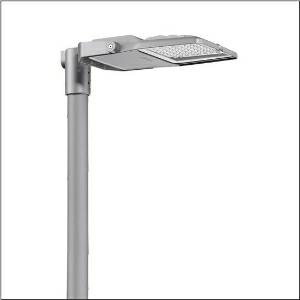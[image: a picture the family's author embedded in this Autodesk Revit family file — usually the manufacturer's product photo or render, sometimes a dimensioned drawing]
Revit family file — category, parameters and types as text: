
# Revit family: floodlight_fl_21_mini___pl52_5xa7776c2d3a_1d2c
name_source: partatom
category: Lighting Fixtures
units: mm (PartAtom-declared; Revit-internal decimal feet)

## family parameters
Cut with Voids When Loaded = No
Host = Face
Light Source = No
Part Type = Normal
Room Calculation Point = No
Round Connector Dimension = Use Diameter
Shared = No

## types (1)
- --- (1 x LED, 12190 lm, 89 W, 3000K)
    Apparent Load = 89 VA
    CIE Flux Codes = 26 60 98 100 100
    Color Rendering = 70
    Color Temperature = 3000K
    Default Elevation = 1800 mm
    Description = Floodlight FL 21 mini, floodlight, primary light control with lens, of PMMA, primary optical cover: protective disc, of toughened safety glass, transparent, light distribution: PL52, light emission: direct distribution, installation type: surface-mounted, LED, High Power LED, rated luminous flux: 12.190lm, luminous efficacy: 137lm/W, light colour: 730, colour temperature: 3000K, control gear: Smart Interface (Zhaga), control: flexible luminous flux parameterisation, time-dependent luminous flux control, constant luminous flux control, overheat protection, pre-setting: logarithmic dimming characteristic, with terminal, 6-pole, mains connection: 220..240V, AC, 50/60Hz, start of lifetime: 89W, end of service life: 94W, reduction: 43W, luminaire housing, of diecast aluminium, powder-coated, SITECO metallic grey (DB 702S), corrosivity category C5 mid according to DIN EN ISO 12944, suitable for swimming pools, chlorine-resistant, sealing non-destructively replaceable, please order mast flange separately, mast bracket, of steel, galvanised, powder-coated, SITECO metallic grey (DB 702S), Smart Interface below and above, protection rating (complete): IP66, insulation class (complete): insulation class II (safety insulation), certification: CE, ENEC, VDE, protection symbol: D, impact resistance: IK08, permissible operating ambient temperature: -40..+40°C, permissible operating ambient temperature for outdoor applications: -40..+50°C, standard: DIN EN 12944, LABS conformity tested according to VDMA 24364:2018-05, packaging unit: 1 piece

Light Distribution: PL52
    Height = 70 mm
    Lamp = 1 x LED
    Lamp Light Flux = 12190 lm
    Lamp Power = 89 W
    Lamp count = 1
    Length = 485 mm
    Luminous efficacy = 137 lm/W
    Manufacturer = Siteco
    ModVariant = No
    Model = 5XA7776C2D3A
    Number of Poles = 1
    OnlyDefault = Yes
    Power Factor = 1
    Product Name = Floodlight FL 21 mini | PL52
    Product group = floodlight | pylon annexe
    ProductGroupID = 6201
    Protection Class = Protection class II
    Protection Degree = IP 66
    RLX_Detail_Level = 1
    RLX_Emergency_Light_Flux = 0 lm
    RLX_Emergency_Type = 0
    RLX_Emergency_Type_DB = No
    RlxData = <blob elided: 101329 chars, md5=cfb7b832>
    Socket = socket
    Standby Power = 0 W
    System Light Flux = 12190 lm
    System Power = 89 W
    Type Comments = factory setting: luminous flux: 100 % | dim-lin: 254 | 456 mA
    Type Image = l_1007125.jpg
    URL = http://relux.com
    VarID = @adj_162719
    Voltage = 0 V
    Weight = 0.00 kg
    Width = 337 mm

## geometry (parser evidence)
native form markers: Blend x4, Sweep x13
no freeform markers — native parametric forms only
